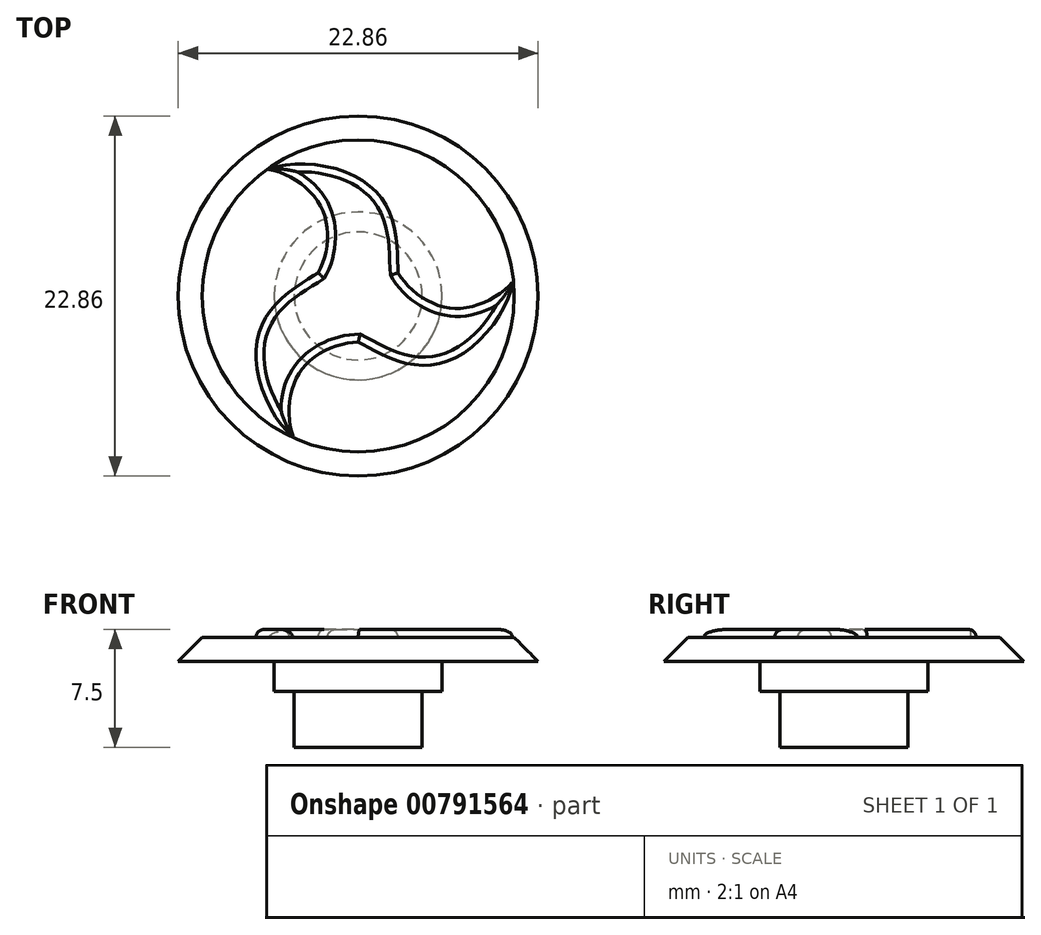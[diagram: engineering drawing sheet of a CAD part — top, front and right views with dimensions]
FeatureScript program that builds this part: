
annotation { "Feature Type Name" : "Feature", "Feature Type Description" : "" }
export const myFeature = defineFeature(function(context is Context, id is Id, definition is map)
    precondition{}
    {
        {
            var Q0;
            Q0=qCreatedBy(makeId("Top.planeOp"),FACE);
            var sketch = newSketch(context, id + "F0", { "sketchPlane" : qUnion([Q0])});
            skCircle(sketch, "E0", {"center": v(0, 0) * mm, "radius": 4.06 * mm});
            skSolve(sketch);
        }
        {
            var Q0;
            Q0=qSketchRegion(id+"F0",true);
            extrude(context, id + "F1", {"entities" : qUnion([Q0]), "depth" : 4.32 * mm, "offsetDistance" : 25.4 * mm, "hasSecondDirection" : true, "secondDirectionOppositeDirection" : true, "secondDirectionDepth" : 1.9 * mm});
        }
        {
            var Q0;
            Q0=qCreatedBy(makeId("Top.planeOp"),FACE);
            var sketch = newSketch(context, id + "F2", { "sketchPlane" : qUnion([Q0])});
            skCircle(sketch, "E1", {"center": v(0, 0) * mm, "radius": 11.43 * mm});
            skSolve(sketch);
        }
        {
            var Q0;
            Q0=qSketchRegion(id+"F2",true);
            extrude(context, id + "F3", {"entities" : qUnion([Q0]), "operationType" : NewBodyOperationType.ADD, "depth" : 5.08 * mm, "offsetDistance" : 25.4 * mm, "hasSecondDirection" : true, "secondDirectionOppositeDirection" : false, "secondDirectionDepth" : 3.56 * mm});
        }
        {
            var Q0;
            Q0=makeQuery(id+"F3.opExtrude","CAP_FACE",FACE,{"disambiguationData":[OSD([sQuery(id+"F2.wireOp",EDGE,"E1")])],"isStart":false});
            var sketch = newSketch(context, id + "F4", { "sketchPlane" : qUnion([Q0])});
            skLineSegment(sketch, "E2", {"start": v(0, 13.85) * mm, "end": v(0, -12.04) * mm, "construction": true});
            skFitSpline(sketch, "E3.MirrorCS", {"points": [v(2.54, 1.47) * mm, v(2.21, 4.66) * mm, v(-0.44, 7.72) * mm, v(-5.64, 8.04) * mm], "startDerivative": vector(-0.42, 6.66) * mm, "endDerivative": vector(-10.01, -4.69) * mm});
            skFitSpline(sketch, "E4.MirrorCS", {"points": [v(-5.64, 8.04) * mm, v(-3.1, 6.67) * mm, v(-1.96, 4.21) * mm, v(-2.54, 1.47) * mm], "startDerivative": vector(6.98, -1.07) * mm, "endDerivative": vector(-3.76, -6.3) * mm});
            skFitSpline(sketch, "E5.MirrorCS", {"points": [v(-2.54, 1.47) * mm, v(-5.14, -0.41) * mm, v(-6.47, -4.24) * mm, v(-4.14, -8.9) * mm], "startDerivative": vector(-5.56, -3.7) * mm, "endDerivative": vector(9.07, -6.33) * mm});
            skFitSpline(sketch, "E6.MirrorCS", {"points": [v(-4.14, -8.9) * mm, v(-4.23, -6.03) * mm, v(-2.67, -3.8) * mm, v(0, -2.93) * mm], "startDerivative": vector(-2.56, 6.58) * mm, "endDerivative": vector(7.34, -0.1) * mm});
            skFitSpline(sketch, "E7.MirrorCS", {"points": [v(0, -2.93) * mm, v(2.93, -4.25) * mm, v(6.9, -3.48) * mm, v(9.78, 0.87) * mm], "startDerivative": vector(5.98, -2.97) * mm, "endDerivative": vector(0.94, 11.01) * mm});
            skFitSpline(sketch, "E8.MirrorCS", {"points": [v(9.78, 0.87) * mm, v(7.33, -0.65) * mm, v(4.63, -0.4) * mm, v(2.54, 1.47) * mm], "startDerivative": vector(-4.42, -5.5) * mm, "endDerivative": vector(-3.58, 6.41) * mm});
            skSolve(sketch);
        }
        {
            var Q0;
            Q0=makeQuery(id+"F4.imprint","IMPRINT",FACE,{"disambiguationData":[TD([[makeQuery(id+"F4.imprint","IMPRINT",EDGE,{"derivedFrom":sQuery(id+"F4.wireOp",EDGE,"E3.MirrorCS")}),1.0]])]});
            extrude(context, id + "F5", {"entities" : qUnion([Q0]), "operationType" : NewBodyOperationType.ADD, "depth" : 0.5 * mm, "offsetDistance" : 25.4 * mm});
        }
        {
            var Q0;
            Q0=makeQuery(id+"F5.opExtrude","CAP_EDGE",EDGE,{"disambiguationData":[OSD([sQuery(id+"F4.wireOp",EDGE,"540d7870-1b1d-4a8b-a01a-0649ee8d1dc2")])],"isStart":false});
            var Q1;
            Q1=makeQuery(id+"F5.opExtrude","CAP_EDGE",EDGE,{"disambiguationData":[OSD([sQuery(id+"F4.wireOp",EDGE,"aba42b5e-28b0-470e-a231-125fee08e634")])],"isStart":false});
            var Q2;
            Q2=makeQuery(id+"F5.opExtrude","CAP_EDGE",EDGE,{"disambiguationData":[OSD([sQuery(id+"F4.wireOp",EDGE,"0776466c-7e87-4a14-b1aa-6b8a6ed35d4c")])],"isStart":false});
            var Q3;
            Q3=makeQuery(id+"F5.opExtrude","CAP_EDGE",EDGE,{"disambiguationData":[OSD([sQuery(id+"F4.wireOp",EDGE,"1ed3ffd7-aa8f-4d2a-9465-77fce45e2a0f")])],"isStart":false});
            var Q4;
            Q4=makeQuery(id+"F5.opExtrude","CAP_EDGE",EDGE,{"disambiguationData":[OSD([sQuery(id+"F4.wireOp",EDGE,"fa8d9906-cd1c-41ad-84ab-4f0bb7fc2a1d")])],"isStart":false});
            var Q5;
            Q5=makeQuery(id+"F5.opExtrude","CAP_EDGE",EDGE,{"disambiguationData":[OSD([sQuery(id+"F4.wireOp",EDGE,"12ae8a38-7c67-4d73-b898-0f337d5ef7bf")])],"isStart":false});
            var Q6;
            Q6=makeQuery(id+"F5.opExtrude","CAP_EDGE",EDGE,{"disambiguationData":[OSD([sQuery(id+"F4.wireOp",EDGE,"E7.MirrorCS")])],"isStart":false});
            var Q7;
            Q7=makeQuery(id+"F5.opExtrude","CAP_EDGE",EDGE,{"disambiguationData":[OSD([sQuery(id+"F4.wireOp",EDGE,"E6.MirrorCS")])],"isStart":false});
            var Q8;
            Q8=makeQuery(id+"F5.opExtrude","CAP_EDGE",EDGE,{"disambiguationData":[OSD([sQuery(id+"F4.wireOp",EDGE,"E8.MirrorCS")])],"isStart":false});
            var Q9;
            Q9=makeQuery(id+"F5.opExtrude","CAP_EDGE",EDGE,{"disambiguationData":[OSD([sQuery(id+"F4.wireOp",EDGE,"E3.MirrorCS")])],"isStart":false});
            var Q10;
            Q10=makeQuery(id+"F5.opExtrude","CAP_EDGE",EDGE,{"disambiguationData":[OSD([sQuery(id+"F4.wireOp",EDGE,"E4.MirrorCS")])],"isStart":false});
            var Q11;
            Q11=makeQuery(id+"F5.opExtrude","CAP_EDGE",EDGE,{"disambiguationData":[OSD([sQuery(id+"F4.wireOp",EDGE,"E5.MirrorCS")])],"isStart":false});
            fillet(context, id + "F6", {"entities" : qUnion([Q0, Q1, Q2, Q3, Q4, Q5, Q6, Q7, Q8, Q9, Q10, Q11]), "radius" : 0.5 * mm, "tangentPropagation" : true, "allowEdgeOverflow" : false});
        }
        {
            var Q0;
            Q0=makeQuery(id+"F3.opExtrude","CAP_EDGE",EDGE,{"disambiguationData":[OSD([sQuery(id+"F2.wireOp",EDGE,"E1")])],"isStart":false});
            chamfer(context, id + "F7", {"entities" : qUnion([Q0]), "width" : 1.52 * mm, "tangentPropagation" : true});
        }
        {
            var Q0;
            Q0=makeQuery(id+"F3.opExtrude","CAP_FACE",FACE,{"disambiguationData":[OSD([sQuery(id+"F2.wireOp",EDGE,"E1")])],"isStart":true});
            var sketch = newSketch(context, id + "F8", { "sketchPlane" : qUnion([Q0])});
            skCircle(sketch, "E9", {"center": v(0, 0) * mm, "radius": 5.33 * mm});
            skSolve(sketch);
        }
        {
            var Q0;
            Q0=makeQuery(id+"F8.imprint","IMPRINT",FACE,{"disambiguationData":[TD([[makeQuery(id+"F8.imprint","IMPRINT",EDGE,{"derivedFrom":sQuery(id+"F8.wireOp",EDGE,"E9")}),1.0]])]});
            extrude(context, id + "F9", {"entities" : qUnion([Q0]), "operationType" : NewBodyOperationType.ADD, "depth" : 1.9 * mm, "offsetDistance" : 25.4 * mm});
        }
    });
